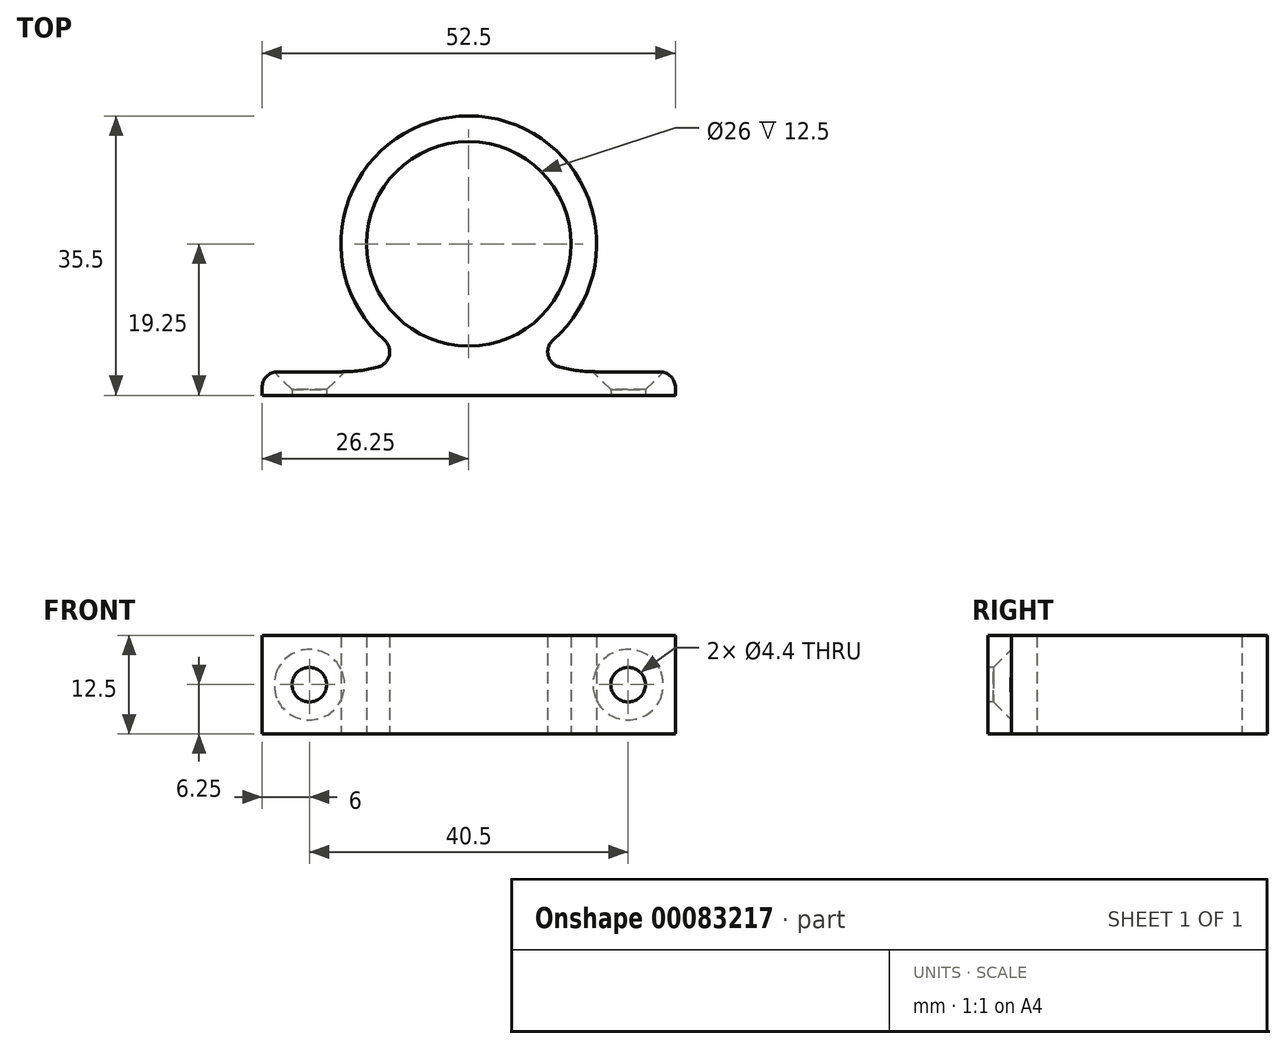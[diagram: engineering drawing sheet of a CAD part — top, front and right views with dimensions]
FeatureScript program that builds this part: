
annotation { "Feature Type Name" : "Feature", "Feature Type Description" : "" }
export const myFeature = defineFeature(function(context is Context, id is Id, definition is map)
    precondition{}
    {
        {
            assignVariable(context, id + "F0", {"name" : "h", "anyValue" : 12.5});
        }
        {
            var Q0;
            Q0=qCreatedBy(makeId("Top.planeOp"),FACE);
            var sketch = newSketch(context, id + "F1", { "sketchPlane" : qUnion([Q0])});
            skCircle(sketch, "E0", {"center": v(0, 0) * mm, "radius": 16.25 * mm});
            skCircle(sketch, "E1", {"center": v(0, 0) * mm, "radius": 13 * mm});
            skLineSegment(sketch, "E2", {"start": v(-16.25, 0) * mm, "end": v(16.25, 0) * mm, "construction": true});
            skLineSegment(sketch, "E3", {"start": v(16.25, 0) * mm, "end": v(16.25, -19.25) * mm});
            skLineSegment(sketch, "E4", {"start": v(16.25, -19.25) * mm, "end": v(-16.25, -19.25) * mm});
            skLineSegment(sketch, "E5", {"start": v(-16.25, -19.25) * mm, "end": v(-16.25, 0) * mm});
            skLineSegment(sketch, "E6", {"start": v(-16.25, -19.25) * mm, "end": v(-26.25, -19.25) * mm});
            skLineSegment(sketch, "E7", {"start": v(-26.25, -19.25) * mm, "end": v(-26.25, -16.25) * mm});
            skLineSegment(sketch, "E8", {"start": v(-26.25, -16.25) * mm, "end": v(-16.25, -16.25) * mm});
            skLineSegment(sketch, "E9", {"start": v(16.25, -19.25) * mm, "end": v(26.25, -19.25) * mm});
            skLineSegment(sketch, "E10", {"start": v(26.25, -19.25) * mm, "end": v(26.25, -16.25) * mm});
            skLineSegment(sketch, "E11", {"start": v(26.25, -16.25) * mm, "end": v(16.25, -16.25) * mm});
            skLineSegment(sketch, "E12", {"start": v(-16.25, 2.74) * mm, "end": v(16.25, 2.74) * mm, "construction": true});
            skCircle(sketch, "E13", {"center": v(-16.25, 2.74) * mm, "radius": 18.99 * mm});
            skCircle(sketch, "E14", {"center": v(16.25, 2.74) * mm, "radius": 18.99 * mm});
            skSolve(sketch);
        }
        {
            var Q0;
            {var subQ0=sQuery(id+"F1.wireOp",EDGE,"E6");Q0=makeQuery(id+"F1.imprint","IMPRINT",FACE,{"disambiguationData":[TD([[makeQuery(id+"F1.imprint","IMPRINT",EDGE,{"derivedFrom":subQ0}),-1.0]])]});}
            var Q1;
            {var subQ1=sQuery(id+"F1.wireOp",EDGE,"E4");Q1=makeQuery(id+"F1.imprint","IMPRINT",FACE,{"disambiguationData":[TD([[makeQuery(id+"F1.imprint","IMPRINT",EDGE,{"derivedFrom":subQ1}),-1.0]])]});}
            var Q2;
            {var subQ0=sQuery(id+"F1.wireOp",EDGE,"E9");Q2=makeQuery(id+"F1.imprint","IMPRINT",FACE,{"disambiguationData":[TD([[makeQuery(id+"F1.imprint","IMPRINT",EDGE,{"derivedFrom":subQ0}),1.0]])]});}
            var Q3;
            {var subQ0=sQuery(id+"F1.wireOp",EDGE,"E13");var subQ1=sQuery(id+"F1.wireOp",EDGE,"E0");var subQ2=makeQuery(id+"F1.imprint","INTERSECT",VERTEX,{"disambiguationData":[OD(1.0)],"derivedFrom":[subQ1,subQ0]});Q3=makeQuery(id+"F1.imprint","IMPRINT",FACE,{"disambiguationData":[TD([[makeQuery(id+"F1.imprint","IMPRINT",EDGE,{"disambiguationData":[TD([[subQ2,-1.0]])],"derivedFrom":subQ1}),1.0]])]});}
            var Q4;
            {var subQ0=sQuery(id+"F1.wireOp",EDGE,"E14");var subQ1=sQuery(id+"F1.wireOp",EDGE,"E0");var subQ2=makeQuery(id+"F1.imprint","INTERSECT",VERTEX,{"disambiguationData":[OD(0.0)],"derivedFrom":[subQ1,subQ0]});Q4=makeQuery(id+"F1.imprint","IMPRINT",FACE,{"disambiguationData":[TD([[makeQuery(id+"F1.imprint","IMPRINT",EDGE,{"disambiguationData":[TD([[subQ2,-1.0]])],"derivedFrom":subQ1}),1.0]])]});}
            var Q5;
            {var subQ5=sQuery(id+"F1.wireOp",EDGE,"E0");var subQ6=makeQuery(id+"F1.imprint","INTERSECT",VERTEX,{"derivedFrom":[subQ5,sQuery(id+"F1.wireOp",EDGE,"E3")]});Q5=makeQuery(id+"F1.imprint","IMPRINT",FACE,{"disambiguationData":[TD([[makeQuery(id+"F1.imprint","IMPRINT",EDGE,{"disambiguationData":[TD([[subQ6,-1.0]])],"derivedFrom":subQ5}),1.0]])]});}
            var Q6;
            {var subQ0=sQuery(id+"F1.wireOp",EDGE,"E13");var subQ1=sQuery(id+"F1.wireOp",EDGE,"E0");var subQ2=makeQuery(id+"F1.imprint","INTERSECT",VERTEX,{"disambiguationData":[OD(0.0)],"derivedFrom":[subQ1,subQ0]});Q6=makeQuery(id+"F1.imprint","IMPRINT",FACE,{"disambiguationData":[TD([[makeQuery(id+"F1.imprint","IMPRINT",EDGE,{"disambiguationData":[TD([[subQ2,-1.0]])],"derivedFrom":subQ1}),1.0]])]});}
            var Q7;
            {var subQ5=sQuery(id+"F1.wireOp",EDGE,"V2IXxMCd-hVSn-ojtk-P72h-iAiq45edRNec");Q7=makeQuery(id+"F1.imprint","IMPRINT",FACE,{"disambiguationData":[TD([[makeQuery(id+"F1.imprint","IMPRINT",EDGE,{"derivedFrom":subQ5}),-1.0]])]});}
            extrude(context, id + "F2", {"entities" : qUnion([Q0, Q1, Q2, Q3, Q4, Q5, Q6, Q7]), "depth" : (getVariable(context, 'h')) * mm});
        }
        {
            var Q0;
            Q0=makeQuery(id+"F2.opExtrude","SWEPT_EDGE",EDGE,{"disambiguationData":[OSD([sQuery(id+"F1.wireOp",EDGE,"E1"),sQuery(id+"F1.wireOp",EDGE,"Uqd4Ytld-iFCL-1tMr-9Fsh-eLRqxmMynze2")])]});
            var Q1;
            Q1=makeQuery(id+"F2.opExtrude","SWEPT_EDGE",EDGE,{"disambiguationData":[OSD([sQuery(id+"F1.wireOp",EDGE,"E1"),sQuery(id+"F1.wireOp",EDGE,"V2IXxMCd-hVSn-ojtk-P72h-iAiq45edRNec")])]});
            var Q2;
            Q2=makeQuery(id+"F2.opExtrude","SWEPT_EDGE",EDGE,{"disambiguationData":[OSD([sQuery(id+"F1.wireOp",EDGE,"E0"),sQuery(id+"F1.wireOp",EDGE,"E13")])]});
            var Q3;
            Q3=makeQuery(id+"F2.opExtrude","SWEPT_EDGE",EDGE,{"disambiguationData":[OSD([sQuery(id+"F1.wireOp",EDGE,"E0"),sQuery(id+"F1.wireOp",EDGE,"E14")])]});
            var Q4;
            Q4=makeQuery(id+"F2.opExtrude","SWEPT_EDGE",EDGE,{"disambiguationData":[OSD([sQuery(id+"F1.wireOp",EDGE,"E10"),sQuery(id+"F1.wireOp",EDGE,"E11")])]});
            var Q5;
            Q5=makeQuery(id+"F2.opExtrude","SWEPT_EDGE",EDGE,{"disambiguationData":[OSD([sQuery(id+"F1.wireOp",EDGE,"E7"),sQuery(id+"F1.wireOp",EDGE,"E8")])]});
            fillet(context, id + "F3", {"entities" : qUnion([Q0, Q1, Q2, Q3, Q4, Q5]), "radius" : 2 * mm, "tangentPropagation" : true, "allowEdgeOverflow" : false});
        }
        {
            var Q0;
            Q0=makeQuery(id+"F2.opExtrude","SWEPT_FACE",FACE,{"disambiguationData":[OSD([sQuery(id+"F1.wireOp",EDGE,"E11")])]});
            var sketch = newSketch(context, id + "F4", { "sketchPlane" : qUnion([Q0])});
            skLineSegment(sketch, "E15", {"start": v(-24.25, 6.25) * mm, "end": v(36.75, 6.25) * mm, "construction": true});
            skPoint(sketch, "E16", {"position": v(-20.25, 6.25) * mm});
            skPoint(sketch, "E17", {"position": v(20.25, 6.25) * mm});
            skSolve(sketch);
        }
        {
            var Q0;
            Q0=sQuery(id+"F4.wireOp",VERTEX,"E17");
            var Q1;
            Q1=sQuery(id+"F4.wireOp",VERTEX,"E16");
            var Q2;
            Q2=makeQuery(id+"F2.opExtrude","SWEPT_BODY",BODY,{"disambiguationData":[OSD([sQuery(id+"F1.wireOp",EDGE,"E0"),sQuery(id+"F1.wireOp",EDGE,"E1"),sQuery(id+"F1.wireOp",EDGE,"E4"),sQuery(id+"F1.wireOp",EDGE,"E6"),sQuery(id+"F1.wireOp",EDGE,"E7"),sQuery(id+"F1.wireOp",EDGE,"E8"),sQuery(id+"F1.wireOp",EDGE,"E9"),sQuery(id+"F1.wireOp",EDGE,"E10"),sQuery(id+"F1.wireOp",EDGE,"E11"),sQuery(id+"F1.wireOp",EDGE,"E13"),sQuery(id+"F1.wireOp",EDGE,"E14"),sQuery(id+"F1.wireOp",EDGE,"V2IXxMCd-hVSn-ojtk-P72h-iAiq45edRNec"),sQuery(id+"F1.wireOp",EDGE,"Uqd4Ytld-iFCL-1tMr-9Fsh-eLRqxmMynze2")])]});
            hole(context, id + "F5", {"style" : HoleStyle.C_SINK, "endStyle" : HoleEndStyle.BLIND, "standardTappedOrClearance" : lookupTablePath({ "standard" : "ISO", "fit" : "Normal", "size" : "M4", "type" : "Clearance" }), "standardBlindInLast" : lookupTablePath({ "fit" : "Standard", "standard" : "ISO", "size" : "M4", "type" : "Clearance" }), "holeDiameter" : 4.4 * mm, "cSinkDiameter" : 8.96 * mm, "cSinkAngle" : 90 * degree, "holeDepth" : 12 * mm, "locations" : qUnion([Q0, Q1]), "scope" : qUnion([Q2]), "startStyle" : HoleStartStyle.PART});
        }
    });
